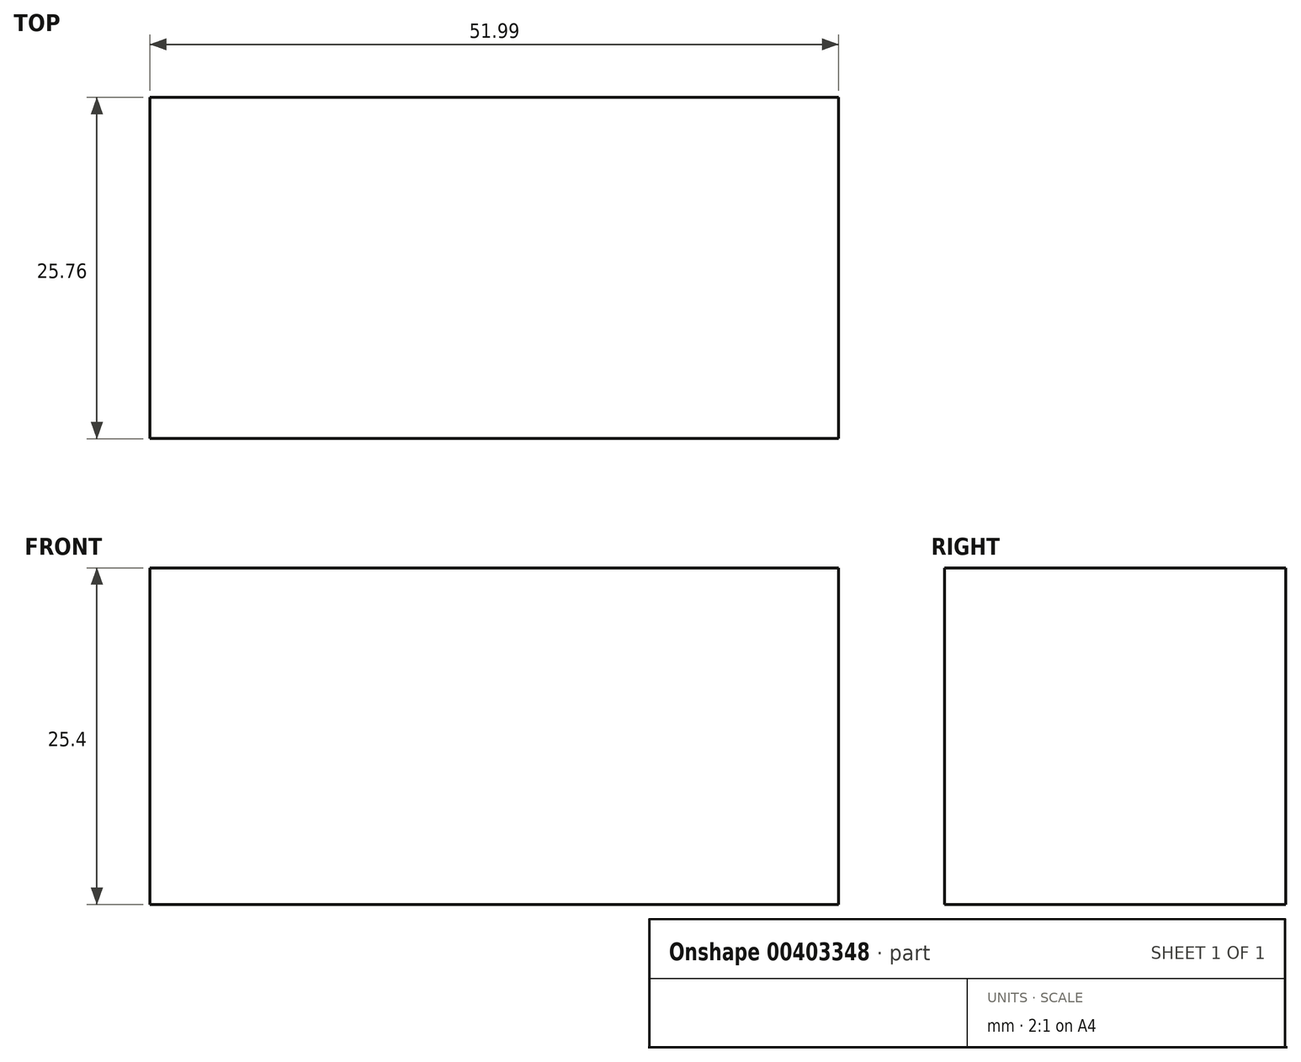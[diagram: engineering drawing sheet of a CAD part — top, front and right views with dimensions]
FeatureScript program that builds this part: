
annotation { "Feature Type Name" : "Feature", "Feature Type Description" : "" }
export const myFeature = defineFeature(function(context is Context, id is Id, definition is map)
    precondition{}
    {
        {
            var Q0;
            Q0=qCreatedBy(makeId("Top.planeOp"),FACE);
            var sketch = newSketch(context, id + "F0", { "sketchPlane" : qUnion([Q0])});
            skLineSegment(sketch, "E0.bottom", {"start": v(-22.84, 3.89) * mm, "end": v(29.15, 3.89) * mm});
            skLineSegment(sketch, "E0.top", {"start": v(-22.84, -21.87) * mm, "end": v(29.15, -21.87) * mm});
            skLineSegment(sketch, "E0.left", {"start": v(-22.84, 3.89) * mm, "end": v(-22.84, -21.87) * mm});
            skLineSegment(sketch, "E0.right", {"start": v(29.15, 3.89) * mm, "end": v(29.15, -21.87) * mm});
            skLineSegment(sketch, "E1", {"start": v(-34.28, 12.9) * mm, "end": v(-20.9, 30.46) * mm});
            skLineSegment(sketch, "E2", {"start": v(-20.9, 30.46) * mm, "end": v(14.9, 30.46) * mm});
            skLineSegment(sketch, "E3", {"start": v(14.9, 30.46) * mm, "end": v(14.9, 12.88) * mm});
            skLineSegment(sketch, "E4", {"start": v(14.9, 12.88) * mm, "end": v(-34.28, 12.88) * mm});
            skSolve(sketch);
        }
        {
            var Q0;
            Q0=makeQuery(id+"F0.imprint","IMPRINT",FACE,{"disambiguationData":[TD([[makeQuery(id+"F0.imprint","IMPRINT",EDGE,{"derivedFrom":sQuery(id+"F0.wireOp",EDGE,"E0.bottom")}),-1.0]])]});
            extrude(context, id + "F1", {"entities" : qUnion([Q0]), "depth" : 25.4 * mm});
        }
    });
